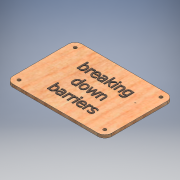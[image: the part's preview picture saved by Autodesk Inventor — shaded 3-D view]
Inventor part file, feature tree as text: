
AUTODESK INVENTOR PART (.ipt)
format: ipt  version: 2016 (Build 200138000, 138)  size: 987,136 bytes
history: native  units: mm
features: extrude x3, sketch x2, other x1, fillet x1
ambient origin geometry x8: Origin, YZ Plane, XZ Plane, XY Plane, X Axis, Y Axis, Z Axis, Center Point
bodies: Solid1 (feature_tree)
feature tree (7):
  other  "FrontPanel.ipt"
  extrude  "Extrusion1"  Depth=3.0mm TaperAngle=0.0deg
  fillet  "Fillet1"  Radius=7.0mm
  sketch  "Sketch2"  dims[d4=1.0mm d5=0.0mm d6=0.5mm d7=0.0mm]
  extrude  "Extrusion2"  Depth=0.5mm TaperAngle=0.0deg
  extrude  "Extrusion3"  [1 undecoded]
  sketch  "Sketch1"  dims[d0=10.0mm d1=3.0mm d2=0.0mm d3=7.0mm]
note: 1 required parameter value undecoded (feature->parameter linkage not recoverable at this tier; creation-order binding heuristic only, values carry confidence <= 0.55)
